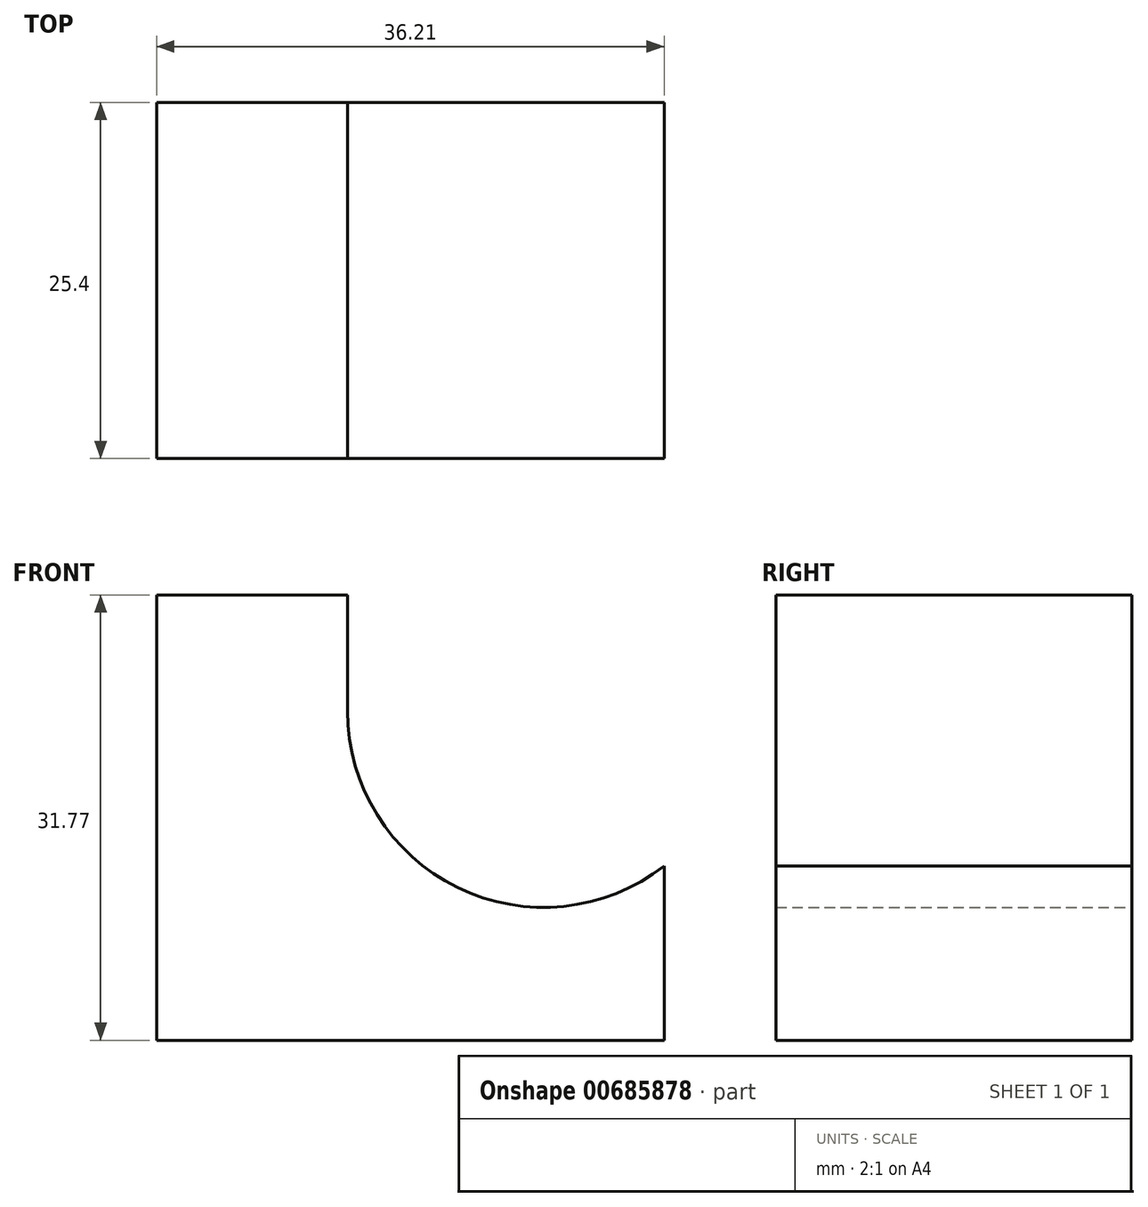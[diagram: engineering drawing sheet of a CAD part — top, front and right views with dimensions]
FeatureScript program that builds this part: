
annotation { "Feature Type Name" : "Feature", "Feature Type Description" : "" }
export const myFeature = defineFeature(function(context is Context, id is Id, definition is map)
    precondition{}
    {
        {
            var Q0;
            Q0=qCreatedBy(makeId("Front.planeOp"),FACE);
            var sketch = newSketch(context, id + "F0", { "sketchPlane" : qUnion([Q0])});
            skLineSegment(sketch, "E0", {"start": v(0, 0) * mm, "end": v(-36.2, 0) * mm});
            skLineSegment(sketch, "E1", {"start": v(-36.2, 0) * mm, "end": v(-36.2, 31.77) * mm});
            skLineSegment(sketch, "E2", {"start": v(-36.2, 31.77) * mm, "end": v(-22.6, 31.77) * mm});
            skLineSegment(sketch, "E3", {"start": v(-22.6, 31.77) * mm, "end": v(-22.6, 23.48) * mm});
            skLineSegment(sketch, "E4", {"start": v(0, 0) * mm, "end": v(0, 12.43) * mm});
            skArc(sketch, "E5", {"start": v(-22.6, 23.48) * mm, "mid": v(-14.74, 10.9) * mm, "end": v(0, 12.43) * mm});
            skSolve(sketch);
        }
        {
            var Q0;
            Q0 = qSketchRegion(id + "F0", true);
            extrude(context, id + "F1", {"entities" : qUnion([Q0]), "depth" : 25.4 * mm, "offsetDistance" : 25.4 * mm});
        }
    });
